FCSTD DOCUMENT  (FreeCAD 1.0R39319 (Git))
Label: Spreadsheet
License: All rights reserved
LicenseURL: https://en.wikipedia.org/wiki/All_rights_reserved
objects: Spreadsheet::Sheet×1

FEATURE [Spreadsheet::Sheet] plane
  cells = A1='CGx; B1='CGz; C1='attack_angle; D1='body_height; E1='body_len; F1='body_span; G1='cannard; H1='cannard_airfoil; I1='cannard_attack_angle; J1='cannard_chord; K1='cannard_len; L1='cannard_start; M1='cannard_thickness; N1='cannard_z_offset; O1='dihedral; P1='foot; Q1='foot_airfoil; R1='foot_base_start; S1='foot_chord; T1='foot_taper; U1='foot_thickness; V1='leading_edge_length; W1='sweep; X1='taper_ratio; Y1='washout; Z1='wing_airfoil_base; AA1='wing_airfoil_tip; AB1='wing_base_start; AC1='wing_chord; AD1='wing_lift; AE1='wing_min_thickness; AF1='winglet_airfoil; AG1='winglet_angle; AH1='winglet_leading_edge_len; AI1='winglet_radius; AJ1='winglet_sections; AK1='winglet_sweep; AL1='winglet_taper_ratio; AM1='winglet_toe; AN1='winglets; AO1='body_airfoil; AP1='scale_y_cannard; AQ1='scale_y_body; AR1='scale_y_wing_base; AS1='scale_y_wing_tip; AT1='scale_y_foot; A2=0.380864988967299; B2=-0.652955252571516; C2(attack_angle)=4.84293471655043; D2(body_height)=0.07; E2(body_len)=0.272050377267532; F2(body_span)=0.12; G2='False; H2='naca0010; I2=1.27710382; J2=0.0504440033; K2=0.15; L2=0.06120297; M2=0.015; N2=0.015; O2(dihedral)=0.188129578574184; P2='False; Q2='naca0012; R2=0; S2=0.06; T2=0.5; U2=0.01; V2(leading_edge_length)=0.45; W2(sweep)=30.3047630572539; X2(taper_ratio)=0.588210796065184; Y2(washout)=-0.341856568534174; Z2(wing_airfoil_base)='sd7032; AA2(wing_airfoil_tip)='naca4415; AB2(wing_base_start)=0.178475088287354; AC2(wing_chord)=0.193507850781326; AD2(wing_lift)=0; AE2=0.015; AF2(winglet_airfoil)='naca0010; AG2(winglet_angle)=-55.1752778261602; AH2(winglet_leading_edge_len)=0.0313467642333606; AI2(winglet_radius)=0.019123632; AJ2=1; AK2(winglet_sweep)=44.3406307771629; AL2(winglet_taper_ratio)=0.904898196910042; AM2(winglet_toe)=1.3458452859836; AN2='True; AO2(body_airfoil)='naca0020; AP2(scale_y_cannard)=2.9728824209193; AQ2(scale_y_body)=1.28621843878477; AR2(scale_y_wing_base)=1; AS2(scale_y_wing_tip)=1; AT2(scale_y_foot)=1.38855639492005; AG3=-55.1752778261602; AM3=1.3458452859836; AF5='winglet_length; AG5='winglet_curve_length; AH5='winglet_curve_end_chord; AF6(winglet_length)==cos(winglet_sweep) * winglet_leading_edge_len * 1000; AG6(winglet_curve_length)==abs(winglet_angle) / 180 * pi * winglet_radius * 1000; AH6(winglet_curve_end_chord)==(1 - (1 - winglet_taper_ratio) * winglet_curve_length / (winglet_curve_length + winglet_length)) * wing_chord * taper_ratio * 1000
